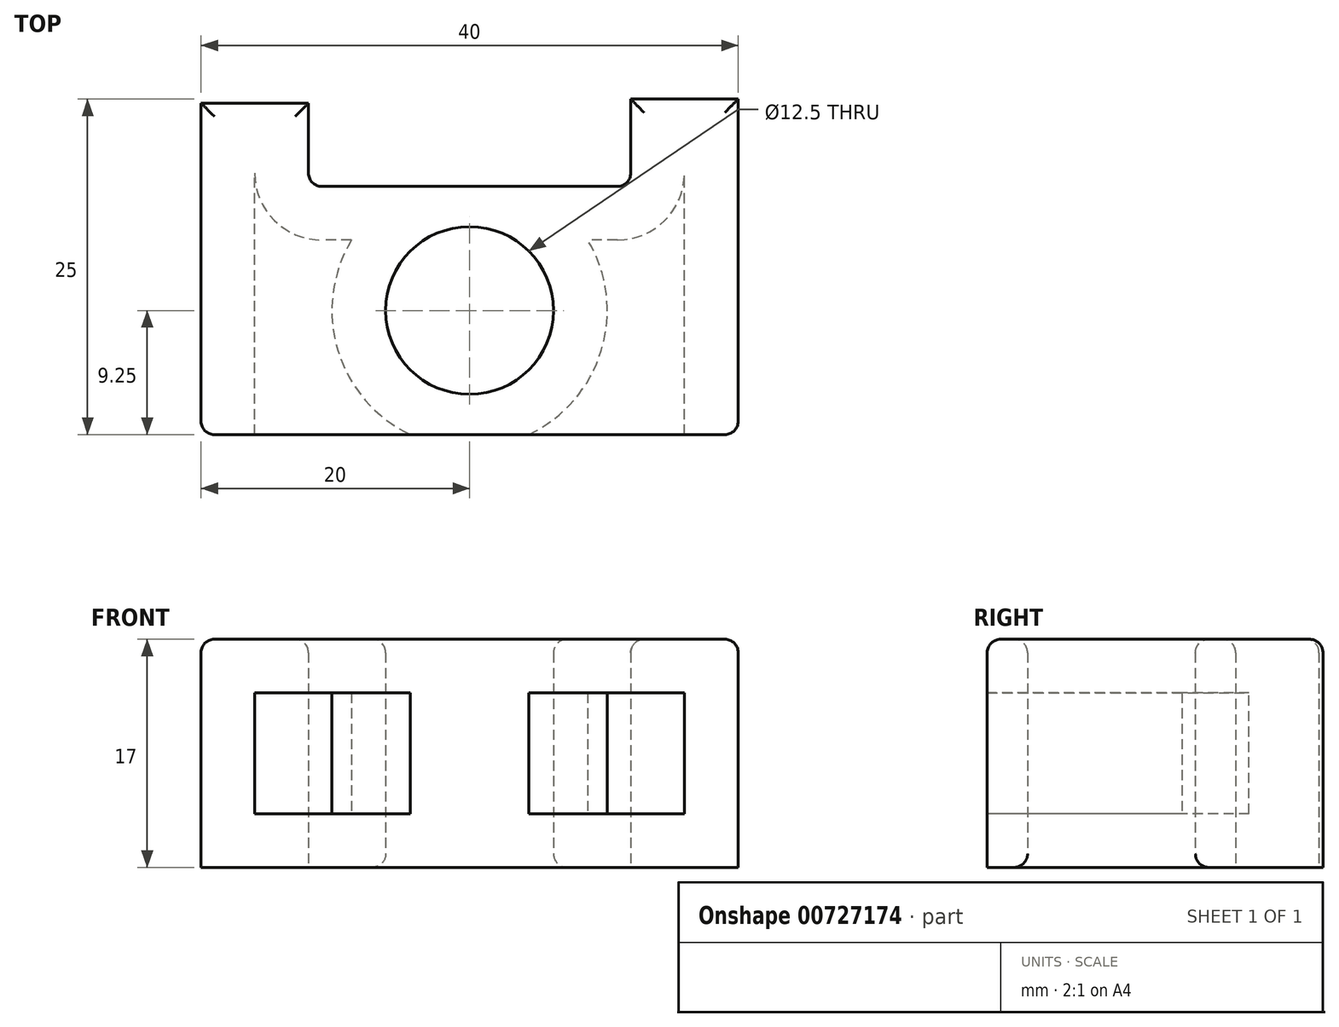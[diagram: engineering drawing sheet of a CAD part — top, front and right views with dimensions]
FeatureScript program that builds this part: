
annotation { "Feature Type Name" : "Feature", "Feature Type Description" : "" }
export const myFeature = defineFeature(function(context is Context, id is Id, definition is map)
    precondition{}
    {
        {
            var Q0;
            Q0=qCreatedBy(makeId("Top.planeOp"),FACE);
            var sketch = newSketch(context, id + "F0", { "sketchPlane" : qUnion([Q0])});
            skLineSegment(sketch, "E0", {"start": v(0, 0) * mm, "end": v(40, 0) * mm});
            skLineSegment(sketch, "E1", {"start": v(40, 0) * mm, "end": v(40, 25) * mm});
            skLineSegment(sketch, "E2", {"start": v(40, 25) * mm, "end": v(32, 25) * mm});
            skLineSegment(sketch, "E3", {"start": v(32, 25) * mm, "end": v(32, 18.5) * mm});
            skLineSegment(sketch, "E4", {"start": v(32, 18.5) * mm, "end": v(8, 18.5) * mm});
            skLineSegment(sketch, "E5", {"start": v(8, 18.5) * mm, "end": v(8, 24.7) * mm});
            skLineSegment(sketch, "E6", {"start": v(8, 24.7) * mm, "end": v(0, 24.7) * mm});
            skLineSegment(sketch, "E7", {"start": v(0, 24.7) * mm, "end": v(0, 0) * mm});
            skLineSegment(sketch, "E8", {"start": v(20, 0) * mm, "end": v(20, 18.5) * mm, "construction": true});
            skCircle(sketch, "E9", {"center": v(20, 9.25) * mm, "radius": 6.25 * mm});
            skSolve(sketch);
        }
        {
            var Q0;
            Q0=makeQuery(id+"F0.imprint","IMPRINT",FACE,{"disambiguationData":[TD([[makeQuery(id+"F0.imprint","IMPRINT",EDGE,{"derivedFrom":sQuery(id+"F0.wireOp",EDGE,"E0")}),1.0]])]});
            extrude(context, id + "F1", {"entities" : qUnion([Q0]), "depth" : 17 * mm, "offsetDistance" : 25 * mm});
        }
        {
            var Q0;
            Q0=makeQuery(id+"F1.opExtrude","CAP_EDGE",EDGE,{"disambiguationData":[OSD([sQuery(id+"F0.wireOp",EDGE,"E4")])],"isStart":false});
            var Q1;
            Q1=makeQuery(id+"F1.opExtrude","CAP_EDGE",EDGE,{"disambiguationData":[OSD([sQuery(id+"F0.wireOp",EDGE,"E3")])],"isStart":false});
            var Q2;
            Q2=makeQuery(id+"F1.opExtrude","SWEPT_EDGE",EDGE,{"disambiguationData":[OSD([sQuery(id+"F0.wireOp",EDGE,"E4"),sQuery(id+"F0.wireOp",EDGE,"E5")])]});
            var Q3;
            Q3=makeQuery(id+"F1.opExtrude","CAP_EDGE",EDGE,{"disambiguationData":[OSD([sQuery(id+"F0.wireOp",EDGE,"E5")])],"isStart":false});
            var Q4;
            Q4=makeQuery(id+"F1.opExtrude","CAP_EDGE",EDGE,{"disambiguationData":[OSD([sQuery(id+"F0.wireOp",EDGE,"E6")])],"isStart":false});
            var Q5;
            Q5=makeQuery(id+"F1.opExtrude","SWEPT_EDGE",EDGE,{"disambiguationData":[OSD([sQuery(id+"F0.wireOp",EDGE,"E3"),sQuery(id+"F0.wireOp",EDGE,"E4")])]});
            var Q6;
            Q6=makeQuery(id+"F1.opExtrude","CAP_EDGE",EDGE,{"disambiguationData":[OSD([sQuery(id+"F0.wireOp",EDGE,"E7")])],"isStart":false});
            var Q7;
            Q7=makeQuery(id+"F1.opExtrude","CAP_EDGE",EDGE,{"disambiguationData":[OSD([sQuery(id+"F0.wireOp",EDGE,"E0")])],"isStart":false});
            var Q8;
            Q8=makeQuery(id+"F1.opExtrude","CAP_EDGE",EDGE,{"disambiguationData":[OSD([sQuery(id+"F0.wireOp",EDGE,"E9")])],"isStart":false});
            var Q9;
            Q9=makeQuery(id+"F1.opExtrude","CAP_EDGE",EDGE,{"disambiguationData":[OSD([sQuery(id+"F0.wireOp",EDGE,"E1")])],"isStart":false});
            var Q10;
            Q10=makeQuery(id+"F1.opExtrude","CAP_EDGE",EDGE,{"disambiguationData":[OSD([sQuery(id+"F0.wireOp",EDGE,"E2")])],"isStart":false});
            var Q11;
            Q11=makeQuery(id+"F1.opExtrude","SWEPT_EDGE",EDGE,{"disambiguationData":[OSD([sQuery(id+"F0.wireOp",EDGE,"E0"),sQuery(id+"F0.wireOp",EDGE,"E7")])]});
            var Q12;
            Q12=makeQuery(id+"F1.opExtrude","SWEPT_EDGE",EDGE,{"disambiguationData":[OSD([sQuery(id+"F0.wireOp",EDGE,"E0"),sQuery(id+"F0.wireOp",EDGE,"E1")])]});
            var Q13;
            Q13=makeQuery(id+"F1.opExtrude","CAP_EDGE",EDGE,{"disambiguationData":[OSD([sQuery(id+"F0.wireOp",EDGE,"E9")])],"isStart":true});
            fillet(context, id + "F2", {"entities" : qUnion([Q0, Q1, Q2, Q3, Q4, Q5, Q6, Q7, Q8, Q9, Q10, Q11, Q12, Q13]), "radius" : 1 * mm, "tangentPropagation" : true, "allowEdgeOverflow" : false});
        }
        {
            var Q0;
            Q0=makeQuery(id+"F1.opExtrude","SWEPT_FACE",FACE,{"disambiguationData":[OSD([sQuery(id+"F0.wireOp",EDGE,"E0")])]});
            shell(context, id + "F3", {"entities" : qUnion([Q0]), "thickness" : 4 * mm});
        }
    });
